# Revit family: Atlas Medical Basin 50cm
name_source: partatom
category: Plumbing Fixtures
units: mm (PartAtom-declared; Revit-internal decimal feet)

## family parameters
Always vertical = Yes
Cut with Voids When Loaded = No
Enable Cutting in Views = No
Host = Wall
Maintain Annotation Orientation = No
OmniClass Number = 23.45.00.00
OmniClass Title = Sanitary, Laundry, and Cleaning Equipment
Part Type = Normal
Room Calculation Point = No
Round Connector Dimension = Use Diameter
Shared = No

## types (2) — shared parameters
Category = Paraplegic / Medical
Ceramic = Ceramic
Colour = White
Manufacturer = Lecico SA
Material = Vitreous China
Silver = Silver
Technical Dimensions = W502 x H177 x D418mm
URL = https://www.lecicosa.co.za
zero-valued in all types: Default Elevation

## per-type parameters (varying)
| type | Product Code |
| Atlas Medical Basin 50cm | ATLBASMED0500UE |
| Atlas Medical Basin 50cm with Bracket | ATLDUOMED0500UE |

note: column(s) folded — value = type name in every type: Model

## geometry (parser evidence)
native form markers: Sweep x4
no freeform markers — native parametric forms only
